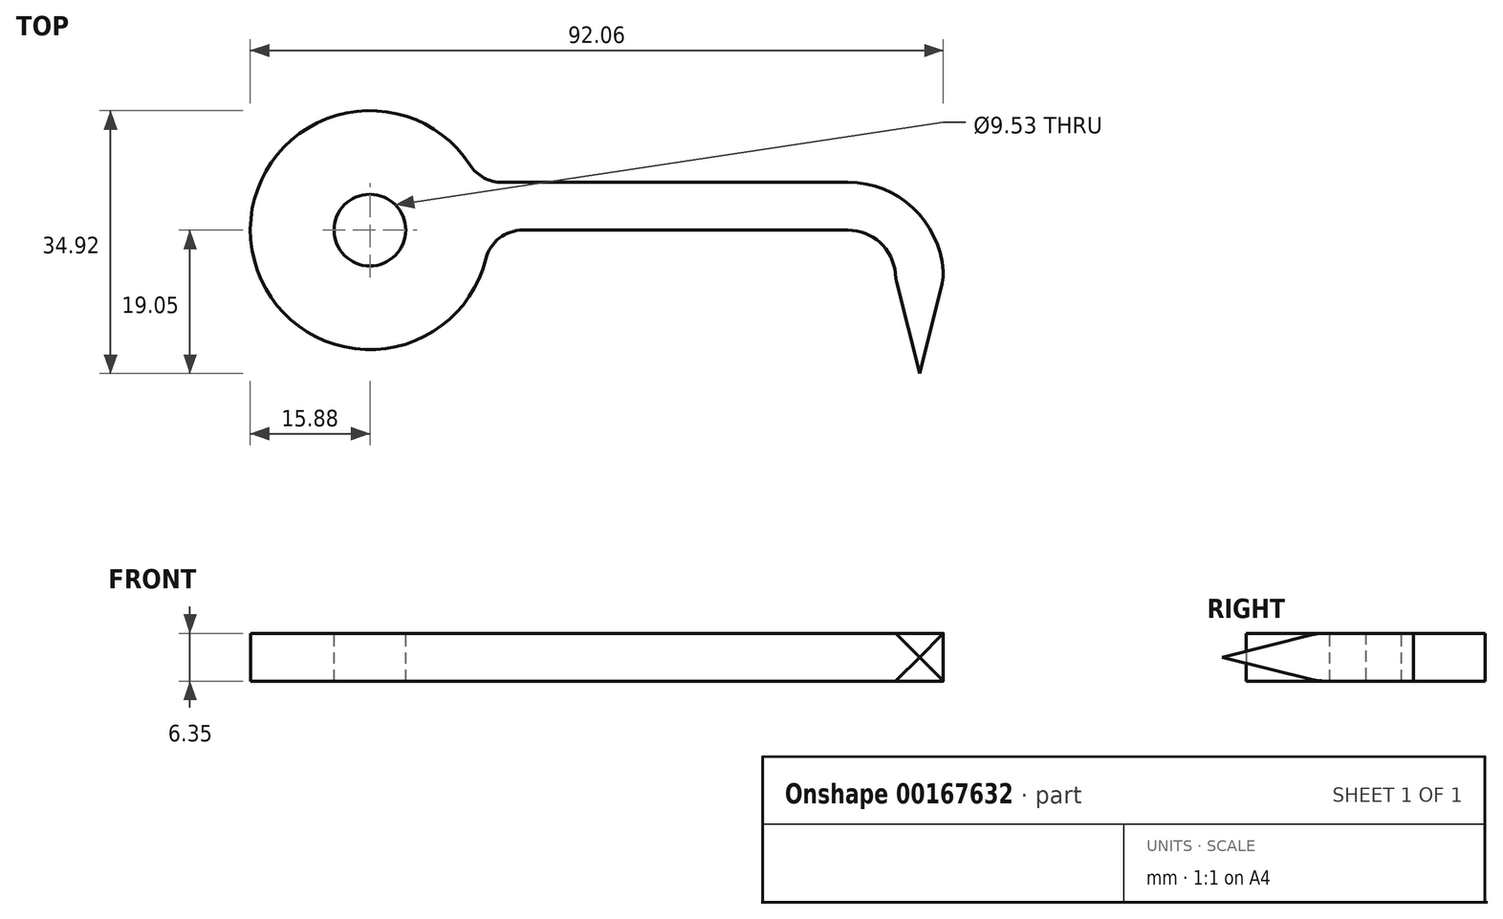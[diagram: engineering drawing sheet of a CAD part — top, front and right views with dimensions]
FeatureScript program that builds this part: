
annotation { "Feature Type Name" : "Feature", "Feature Type Description" : "" }
export const myFeature = defineFeature(function(context is Context, id is Id, definition is map)
    precondition{}
    {
        {
            var Q0;
            Q0=qCreatedBy(makeId("Top.planeOp"),FACE);
            var sketch = newSketch(context, id + "F0", { "sketchPlane" : qUnion([Q0])});
            skCircle(sketch, "E0", {"center": v(0, 0) * mm, "radius": 15.88 * mm});
            skLineSegment(sketch, "E1", {"start": v(0, 0) * mm, "end": v(69.85, 0) * mm});
            skLineSegment(sketch, "E2.0", {"start": v(14.55, 6.35) * mm, "end": v(76.2, 6.35) * mm});
            skLineSegment(sketch, "E3", {"start": v(76.2, 6.35) * mm, "end": v(76.2, -19.05) * mm});
            skLineSegment(sketch, "E4.0", {"start": v(69.85, 0) * mm, "end": v(69.85, -19.05) * mm});
            skLineSegment(sketch, "E5", {"start": v(69.85, -19.05) * mm, "end": v(76.2, -19.05) * mm});
            skPoint(sketch, "E6.orphan", {"position": v(76.2, 0) * mm});
            skSolve(sketch);
        }
        {
            var Q0;
            {var subQ0=sQuery(id+"F0.wireOp",EDGE,"E0");var subQ1=makeQuery(id+"F0.imprint","INTERSECT",VERTEX,{"derivedFrom":[subQ0,sQuery(id+"F0.wireOp",EDGE,"E2.0")]});Q0=makeQuery(id+"F0.imprint","IMPRINT",FACE,{"disambiguationData":[TD([[makeQuery(id+"F0.imprint","IMPRINT",EDGE,{"disambiguationData":[TD([[subQ1,1.0]])],"derivedFrom":subQ0}),1.0]])]});}
            var Q1;
            {var subQ0=sQuery(id+"F0.wireOp",EDGE,"E2.0");Q1=makeQuery(id+"F0.imprint","IMPRINT",FACE,{"disambiguationData":[TD([[makeQuery(id+"F0.imprint","IMPRINT",EDGE,{"derivedFrom":subQ0}),-1.0]])]});}
            extrude(context, id + "F1", {"entities" : qUnion([Q0, Q1]), "depth" : 6.35 * mm});
        }
        {
            var Q0;
            Q0=makeQuery(id+"F1.opExtrude","SWEPT_EDGE",EDGE,{"disambiguationData":[OSD([sQuery(id+"F0.wireOp",EDGE,"E0"),sQuery(id+"F0.wireOp",EDGE,"E1")])]});
            var Q1;
            Q1=makeQuery(id+"F1.opExtrude","SWEPT_EDGE",EDGE,{"disambiguationData":[OSD([sQuery(id+"F0.wireOp",EDGE,"E0"),sQuery(id+"F0.wireOp",EDGE,"E2.0")])]});
            fillet(context, id + "F2", {"entities" : qUnion([Q0, Q1]), "radius" : 5.08 * mm, "tangentPropagation" : true, "allowEdgeOverflow" : false});
        }
        {
            var Q0;
            Q0=makeQuery(id+"F1.opExtrude","SWEPT_EDGE",EDGE,{"disambiguationData":[OSD([sQuery(id+"F0.wireOp",EDGE,"E2.0"),sQuery(id+"F0.wireOp",EDGE,"E3")])]});
            fillet(context, id + "F3", {"entities" : qUnion([Q0]), "radius" : 12.7 * mm, "tangentPropagation" : true, "allowEdgeOverflow" : false});
        }
        {
            var Q0;
            Q0=makeQuery(id+"F1.opExtrude","SWEPT_EDGE",EDGE,{"disambiguationData":[OSD([sQuery(id+"F0.wireOp",EDGE,"E1"),sQuery(id+"F0.wireOp",EDGE,"E4.0")])]});
            fillet(context, id + "F4", {"entities" : qUnion([Q0]), "radius" : 6.35 * mm, "tangentPropagation" : true, "allowEdgeOverflow" : false});
        }
        {
            var Q0;
            Q0=makeQuery(id+"F1.opExtrude","SWEPT_EDGE",EDGE,{"disambiguationData":[OSD([sQuery(id+"F0.wireOp",EDGE,"E3"),sQuery(id+"F0.wireOp",EDGE,"E5")])]});
            var Q1;
            Q1=makeQuery(id+"F1.opExtrude","CAP_EDGE",EDGE,{"disambiguationData":[OSD([sQuery(id+"F0.wireOp",EDGE,"E5")])],"isStart":false});
            var Q2;
            Q2=makeQuery(id+"F1.opExtrude","SWEPT_EDGE",EDGE,{"disambiguationData":[OSD([sQuery(id+"F0.wireOp",EDGE,"E4.0"),sQuery(id+"F0.wireOp",EDGE,"E5")])]});
            var Q3;
            Q3=makeQuery(id+"F1.opExtrude","CAP_EDGE",EDGE,{"disambiguationData":[OSD([sQuery(id+"F0.wireOp",EDGE,"E5")])],"isStart":true});
            chamfer(context, id + "F5", {"entities" : qUnion([Q0, Q1, Q2, Q3]), "chamferType" : ChamferType.TWO_OFFSETS, "width1" : 12.7 * mm, "oppositeDirection" : false, "width2" : 3.17 * mm, "tangentPropagation" : true});
        }
        {
            var Q0;
            {var subQ0=sQuery(id+"F0.wireOp",EDGE,"E3");Q0=makeQuery(id+"F5.opChamfer","BLEND_EDGE",EDGE,{"blendedFrom":[makeQuery(id+"F1.opExtrude","SWEPT_EDGE",EDGE,{"disambiguationData":[OSD([subQ0,sQuery(id+"F0.wireOp",EDGE,"E5")])]}),makeQuery(id+"F3.opFillet","BLEND_FACE",FACE,{"disambiguationData":[OSD([sQuery(id+"F0.wireOp",EDGE,"E2.0"),subQ0])]})],"blendedInto":[makeQuery(id+"F3.opFillet","BLEND_FACE",FACE,{"disambiguationData":[OSD([sQuery(id+"F0.wireOp",EDGE,"E2.0"),subQ0])]})]});}
            var Q1;
            {var subQ0=sQuery(id+"F0.wireOp",EDGE,"E5");Q1=makeQuery(id+"F5.opChamfer","BLEND_EDGE",EDGE,{"blendedFrom":[makeQuery(id+"F1.opExtrude","CAP_EDGE",EDGE,{"disambiguationData":[OSD([subQ0])],"isStart":true}),makeQuery(id+"F1.opExtrude","CAP_FACE",FACE,{"disambiguationData":[OSD([sQuery(id+"F0.wireOp",EDGE,"E0"),sQuery(id+"F0.wireOp",EDGE,"E1"),sQuery(id+"F0.wireOp",EDGE,"E2.0"),sQuery(id+"F0.wireOp",EDGE,"E3"),sQuery(id+"F0.wireOp",EDGE,"E4.0"),subQ0])],"isStart":true})],"blendedInto":[makeQuery(id+"F1.opExtrude","CAP_FACE",FACE,{"disambiguationData":[OSD([sQuery(id+"F0.wireOp",EDGE,"E0"),sQuery(id+"F0.wireOp",EDGE,"E1"),sQuery(id+"F0.wireOp",EDGE,"E2.0"),sQuery(id+"F0.wireOp",EDGE,"E3"),sQuery(id+"F0.wireOp",EDGE,"E4.0"),subQ0])],"isStart":true})]});}
            var Q2;
            {var subQ0=sQuery(id+"F0.wireOp",EDGE,"E5");Q2=makeQuery(id+"F5.opChamfer","BLEND_EDGE",EDGE,{"blendedFrom":[makeQuery(id+"F1.opExtrude","CAP_EDGE",EDGE,{"disambiguationData":[OSD([subQ0])],"isStart":false}),makeQuery(id+"F1.opExtrude","CAP_FACE",FACE,{"disambiguationData":[OSD([sQuery(id+"F0.wireOp",EDGE,"E0"),sQuery(id+"F0.wireOp",EDGE,"E1"),sQuery(id+"F0.wireOp",EDGE,"E2.0"),sQuery(id+"F0.wireOp",EDGE,"E3"),sQuery(id+"F0.wireOp",EDGE,"E4.0"),subQ0])],"isStart":false})],"blendedInto":[makeQuery(id+"F1.opExtrude","CAP_FACE",FACE,{"disambiguationData":[OSD([sQuery(id+"F0.wireOp",EDGE,"E0"),sQuery(id+"F0.wireOp",EDGE,"E1"),sQuery(id+"F0.wireOp",EDGE,"E2.0"),sQuery(id+"F0.wireOp",EDGE,"E3"),sQuery(id+"F0.wireOp",EDGE,"E4.0"),subQ0])],"isStart":false})]});}
            var Q3;
            {var subQ0=sQuery(id+"F0.wireOp",EDGE,"E4.0");Q3=makeQuery(id+"F5.opChamfer","BLEND_EDGE",EDGE,{"blendedFrom":[makeQuery(id+"F1.opExtrude","SWEPT_EDGE",EDGE,{"disambiguationData":[OSD([subQ0,sQuery(id+"F0.wireOp",EDGE,"E5")])]}),makeQuery(id+"F4.opFillet","BLEND_FACE",FACE,{"disambiguationData":[OSD([sQuery(id+"F0.wireOp",EDGE,"E1"),subQ0])]})],"blendedInto":[makeQuery(id+"F4.opFillet","BLEND_FACE",FACE,{"disambiguationData":[OSD([sQuery(id+"F0.wireOp",EDGE,"E1"),subQ0])]})]});}
            fillet(context, id + "F6", {"entities" : qUnion([Q0, Q1, Q2, Q3]), "radius" : 5.08 * mm, "tangentPropagation" : true, "allowEdgeOverflow" : false});
        }
        {
            var Q0;
            Q0=makeQuery(id+"F1.opExtrude","CAP_FACE",FACE,{"disambiguationData":[OSD([sQuery(id+"F0.wireOp",EDGE,"E0"),sQuery(id+"F0.wireOp",EDGE,"E1"),sQuery(id+"F0.wireOp",EDGE,"E2.0"),sQuery(id+"F0.wireOp",EDGE,"E3"),sQuery(id+"F0.wireOp",EDGE,"E4.0"),sQuery(id+"F0.wireOp",EDGE,"E5")])],"isStart":false});
            var sketch = newSketch(context, id + "F7", { "sketchPlane" : qUnion([Q0])});
            skCircle(sketch, "E7", {"center": v(0, 0) * mm, "radius": 4.76 * mm});
            skSolve(sketch);
        }
        {
            var Q0;
            Q0 = qSketchRegion(id + "F7", true);
            extrude(context, id + "F8", {"entities" : qUnion([Q0]), "operationType" : NewBodyOperationType.REMOVE, "endBound" : BoundingType.UP_TO_NEXT, "oppositeDirection" : true, "depth" : 25.4 * mm});
        }
    });
